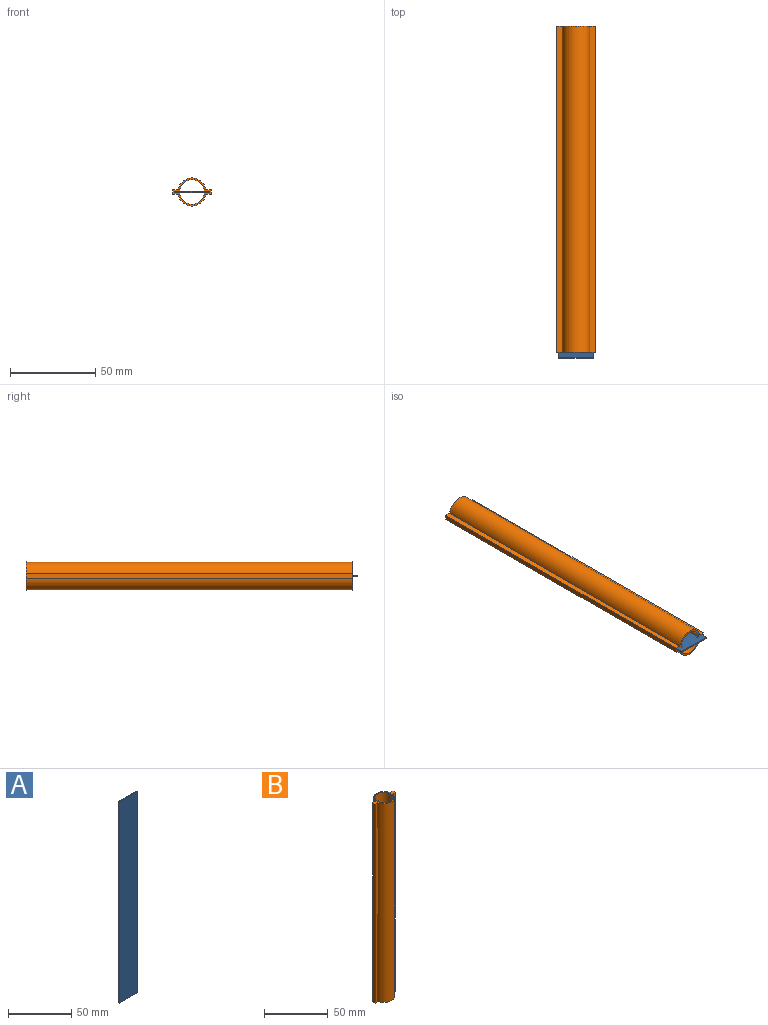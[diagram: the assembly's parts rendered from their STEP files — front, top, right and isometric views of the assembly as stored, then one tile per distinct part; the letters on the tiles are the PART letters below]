
ASSEMBLY  parts=2 mates=1
PART A: 6 faces, bbox 20.5x0.8x195 mm
  f0: plane 195x0.75mm, normal (-1,0,0), area 146.3mm2, adj f1,f3,f4,f5
  f1: plane 195x20.5mm, normal (0,-1,0), area 3997.5mm2, adj f0,f2,f4,f5
  f2: plane 195x0.75mm, normal (1,0,0), area 146.3mm2, adj f1,f3,f4,f5
  f3: plane 195x20.5mm, normal (0,1,0), area 3997.5mm2, adj f0,f2,f4,f5
  f4: plane 20.5x0.75mm, normal (0,0,1), area 15.4mm2, adj f0,f1,f2,f3
  f5: plane 20.5x0.75mm, normal (0,0,-1), area 15.4mm2, adj f0,f1,f2,f3
PART B: 26 faces, bbox 22.5x16.5x191.5 mm
  f0: plane 22.5x16.5mm, normal (0,0,-1), area 60.9mm2, adj f5,f6,f7,f8,f9,f10,f11,f12
  f1: plane 0.99x0.6mm, normal (0,1,0), area 0.6mm2, adj f13,f15,f16,f19
  f2: plane 0.99x0.6mm, normal (0,-1,0), area 0.6mm2, adj f12,f15,f16,f19
  f3: plane 0.99x0.6mm, normal (0,-1,0), area 0.6mm2, adj f12,f15,f17,f18
  f4: plane 0.99x0.6mm, normal (0,1,0), area 0.6mm2, adj f13,f15,f17,f18
  f5: plane 191.5x2.8mm, normal (-1,0,0), area 536.2mm2, adj f0,f6,f14,f15
  f6: plane 191.5x3.12mm, normal (0,-1,0), area 597.4mm2, adj f0,f5,f7,f15
  f7: cylinder r=8.25mm len=191.5mm, axis (0,0,-1), area 4424.5mm2, adj f0,f6,f8,f15
  f8: plane 191.5x3.12mm, normal (0,-1,0), area 597.4mm2, adj f0,f7,f9,f15
  f9: plane 191.5x2.8mm, normal (1,0,0), area 536.2mm2, adj f0,f8,f10,f15
  f10: plane 191.5x3.12mm, normal (0,1,0), area 597.4mm2, adj f0,f9,f11,f15
  f11: cylinder r=8.25mm len=191.5mm, axis (0,0,-1), area 4424.5mm2, adj f0,f10,f14,f15
  f12: cylinder r=7.25mm len=191.5mm, axis (0,0,-1), area 4208.4mm2, adj f0,f2,f3,f15,f22,f24
  f13: cylinder r=7.25mm len=191.5mm, axis (0,0,-1), area 4208.4mm2, adj f0,f1,f4,f15,f20,f23
  f14: plane 191.5x3.12mm, normal (0,1,0), area 597.4mm2, adj f0,f5,f11,f15
  f15: plane 22.5x16.5mm, normal (0,0,1), area 67.3mm2, adj f1,f2,f3,f4,f5,f6,f7,f8
  f16: plane 0.8x0.6mm, normal (-1,0,0), area 0.5mm2, adj f1,f2,f15,f19
  f17: plane 0.8x0.6mm, normal (1,0,0), area 0.5mm2, adj f3,f4,f15,f18
  f18: plane 4x0.8mm, normal (0,0,-1), area 3.2mm2, adj f3,f4,f17,f23,f24,f25
  f19: plane 4x0.8mm, normal (0,0,-1), area 3.2mm2, adj f1,f2,f16,f20,f21,f22
  f20: plane 190.9x3.01mm, normal (0,-1,0), area 574.8mm2, adj f0,f13,f19,f21
  f21: plane 190.9x0.8mm, normal (-1,0,0), area 152.7mm2, adj f0,f19,f20,f22
  f22: plane 190.9x3.01mm, normal (0,1,0), area 574.8mm2, adj f0,f12,f19,f21
  f23: plane 190.9x3.01mm, normal (0,-1,0), area 574.8mm2, adj f0,f13,f18,f25
  f24: plane 190.9x3.01mm, normal (0,1,0), area 574.8mm2, adj f0,f12,f18,f25
  f25: plane 190.9x0.8mm, normal (1,0,0), area 152.7mm2, adj f0,f18,f23,f24
PLACE A rot(axis=(-1,0,0),90deg) t=(-74.43,-19.43,-97.01)mm
PLACE B rot(axis=(1,0,0),90deg) t=(-47.09,35.57,-96.04)mm
MATE slider B.f0 <-> A.f4  axis (0,1,0) through (-36.84,175.57,-95.64)mm
